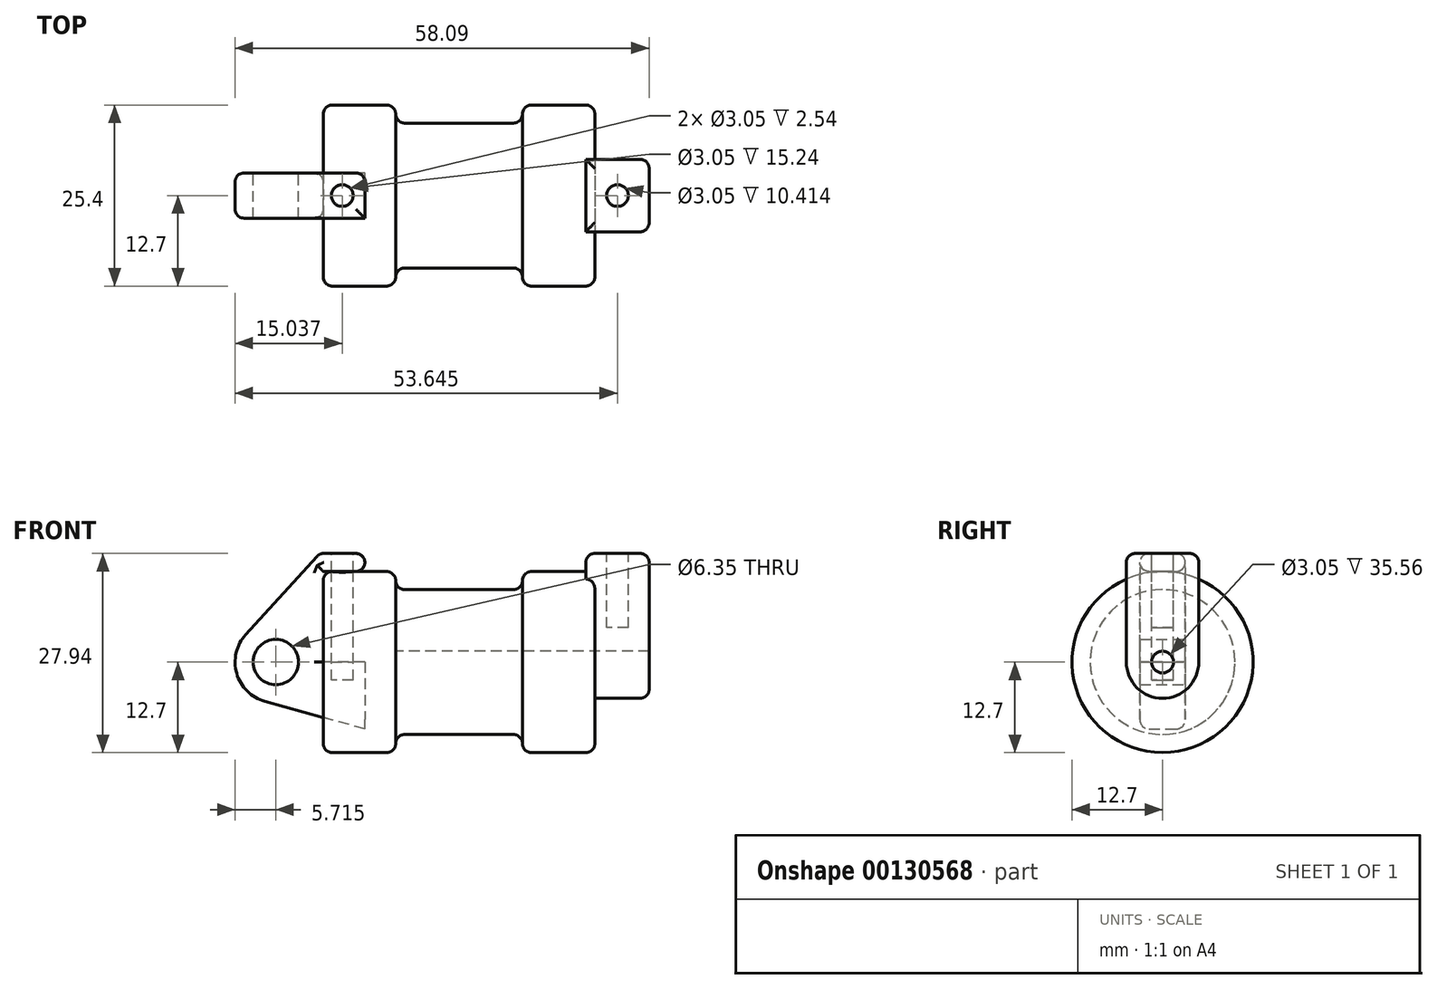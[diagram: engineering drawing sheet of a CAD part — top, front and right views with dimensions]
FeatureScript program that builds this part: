
annotation { "Feature Type Name" : "Feature", "Feature Type Description" : "" }
export const myFeature = defineFeature(function(context is Context, id is Id, definition is map)
    precondition{}
    {
        {
            var Q0;
            Q0=qCreatedBy(makeId("Front.planeOp"),FACE);
            var sketch = newSketch(context, id + "F0", { "sketchPlane" : qUnion([Q0])});
            skLineSegment(sketch, "E0", {"start": v(0, 0) * mm, "end": v(0, 12.7) * mm});
            skLineSegment(sketch, "E1", {"start": v(0, 12.7) * mm, "end": v(10.16, 12.7) * mm});
            skLineSegment(sketch, "E2", {"start": v(10.16, 12.7) * mm, "end": v(10.16, 10.16) * mm});
            skLineSegment(sketch, "E3", {"start": v(10.16, 10.16) * mm, "end": v(27.94, 10.16) * mm});
            skLineSegment(sketch, "E4", {"start": v(27.94, 10.16) * mm, "end": v(27.94, 12.7) * mm});
            skLineSegment(sketch, "E5", {"start": v(27.94, 12.7) * mm, "end": v(38.1, 12.7) * mm});
            skLineSegment(sketch, "E6", {"start": v(38.1, 12.7) * mm, "end": v(38.1, 0) * mm});
            skLineSegment(sketch, "E7", {"start": v(38.1, 0) * mm, "end": v(0, 0) * mm});
            skLineSegment(sketch, "E8", {"start": v(5.84, 15.24) * mm, "end": v(-0.5, 15.24) * mm});
            skLineSegment(sketch, "E9", {"start": v(-0.5, 15.24) * mm, "end": v(-10.88, 3.85) * mm});
            skLineSegment(sketch, "E10", {"start": v(0, 0) * mm, "end": v(-6.65, 0) * mm});
            skCircle(sketch, "E11", {"center": v(-6.65, 0) * mm, "radius": 5.72 * mm});
            skCircle(sketch, "E12", {"center": v(-6.65, 0) * mm, "radius": 3.18 * mm});
            skLineSegment(sketch, "E13", {"start": v(5.84, 15.24) * mm, "end": v(5.84, -9.4) * mm});
            skLineSegment(sketch, "E14", {"start": v(5.84, -9.4) * mm, "end": v(-8.18, -5.5) * mm});
            skSolve(sketch);
        }
        {
            var Q0;
            {var subQ0=sQuery(id+"F0.wireOp",EDGE,"E0");Q0=makeQuery(id+"F0.imprint","IMPRINT",FACE,{"disambiguationData":[TD([[makeQuery(id+"F0.imprint","IMPRINT",EDGE,{"derivedFrom":subQ0}),-1.0]])]});}
            var Q1;
            {var subQ0=sQuery(id+"F0.wireOp",EDGE,"E2");Q1=makeQuery(id+"F0.imprint","IMPRINT",FACE,{"disambiguationData":[TD([[makeQuery(id+"F0.imprint","IMPRINT",EDGE,{"derivedFrom":subQ0}),-1.0]])]});}
            var Q2;
            Q2=sQuery(id+"F0.wireOp",EDGE,"E7");
            revolve(context, id + "F1", {"entities" : qUnion([Q0, Q1]), "axis" : qUnion([Q2]), "revolveType" : RevolveType.FULL});
        }
        {
            var Q0;
            {var subQ3=sQuery(id+"F0.wireOp",EDGE,"E0");Q0=makeQuery(id+"F0.imprint","IMPRINT",FACE,{"disambiguationData":[TD([[makeQuery(id+"F0.imprint","IMPRINT",EDGE,{"derivedFrom":subQ3}),1.0]])]});}
            var Q1;
            {var subQ0=sQuery(id+"F0.wireOp",EDGE,"E14");Q1=makeQuery(id+"F0.imprint","IMPRINT",FACE,{"disambiguationData":[TD([[makeQuery(id+"F0.imprint","IMPRINT",EDGE,{"derivedFrom":subQ0}),-1.0]])]});}
            var Q2;
            {var subQ4=sQuery(id+"F0.wireOp",EDGE,"E12");Q2=makeQuery(id+"F0.imprint","IMPRINT",FACE,{"disambiguationData":[TD([[makeQuery(id+"F0.imprint","IMPRINT",EDGE,{"derivedFrom":subQ4}),-1.0]])]});}
            extrude(context, id + "F2", {"entities" : qUnion([Q0, Q1, Q2]), "endBound" : BoundingType.SYMMETRIC, "depth" : 6.35 * mm});
        }
        {
            var Q0;
            Q0=makeQuery(id+"F1.opRevolve","SWEPT_FACE",FACE,{"disambiguationData":[OSD([sQuery(id+"F0.wireOp",EDGE,"E6")])]});
            var sketch = newSketch(context, id + "F3", { "sketchPlane" : qUnion([Q0])});
            skCircle(sketch, "E15", {"center": v(0, 0) * mm, "radius": 1.52 * mm});
            skCircle(sketch, "E16", {"center": v(0, 0) * mm, "radius": 5.08 * mm});
            skLineSegment(sketch, "E17", {"start": v(-5.08, 0) * mm, "end": v(-5.08, 15.24) * mm});
            skLineSegment(sketch, "E18", {"start": v(5.08, 0) * mm, "end": v(5.08, 15.24) * mm});
            skLineSegment(sketch, "E19", {"start": v(-5.08, 15.24) * mm, "end": v(5.08, 15.24) * mm});
            skSolve(sketch);
        }
        {
            var Q0;
            {var subQ0=sQuery(id+"F3.wireOp",EDGE,"E19");Q0=makeQuery(id+"F3.imprint","IMPRINT",FACE,{"disambiguationData":[TD([[makeQuery(id+"F3.imprint","IMPRINT",EDGE,{"derivedFrom":subQ0}),-1.0]])]});}
            var Q1;
            {var subQ0=sQuery(id+"F3.wireOp",EDGE,"E17");var subQ1=sQuery(id+"F3.wireOp",EDGE,"E16");var subQ2=makeQuery(id+"F3.imprint","INTERSECT",VERTEX,{"derivedFrom":[subQ1,subQ0]});Q1=makeQuery(id+"F3.imprint","IMPRINT",FACE,{"disambiguationData":[TD([[makeQuery(id+"F3.imprint","IMPRINT",EDGE,{"disambiguationData":[TD([[subQ2,1.0]])],"derivedFrom":subQ1}),-1.0]])]});}
            var Q2;
            Q2=makeQuery(id+"F3.imprint","IMPRINT",FACE,{"disambiguationData":[TD([[makeQuery(id+"F3.imprint","IMPRINT",EDGE,{"derivedFrom":sQuery(id+"F3.wireOp",EDGE,"E15")}),-1.0]])]});
            extrude(context, id + "F4", {"entities" : qUnion([Q0, Q1, Q2]), "operationType" : NewBodyOperationType.ADD, "depth" : 7.62 * mm, "hasSecondDirection" : true, "secondDirectionOppositeDirection" : true, "secondDirectionDepth" : 1.27 * mm});
        }
        {
            var Q0;
            Q0=makeQuery(id+"F4.boolean.opBoolean","SPLIT",FACE,{"disambiguationData":[TD([makeQuery(id+"F4.opExtrude","SWEPT_FACE",FACE,{"disambiguationData":[OSD([sQuery(id+"F3.wireOp",EDGE,"E15")])]})])],"derivedFrom":makeQuery(id+"F1.opRevolve","SWEPT_FACE",FACE,{"disambiguationData":[OSD([sQuery(id+"F0.wireOp",EDGE,"E6")])]})});
            var Q1;
            Q1=makeQuery(id+"F1.opRevolve","SWEPT_FACE",FACE,{"disambiguationData":[OSD([sQuery(id+"F0.wireOp",EDGE,"E2")])]});
            extrude(context, id + "F5", {"entities" : qUnion([Q0]), "operationType" : NewBodyOperationType.REMOVE, "endBound" : BoundingType.UP_TO_SURFACE, "oppositeDirection" : true, "endBoundEntityFace" : qUnion([Q1]), "depth" : 25.4 * mm});
        }
        {
            var Q0;
            Q0=makeQuery(id+"F2.opExtrude","SWEPT_FACE",FACE,{"disambiguationData":[OSD([sQuery(id+"F0.wireOp",EDGE,"E8")])]});
            var sketch = newSketch(context, id + "F6", { "sketchPlane" : qUnion([Q0])});
            skCircle(sketch, "E20", {"center": v(2.67, 0) * mm, "radius": 1.52 * mm});
            skPoint(sketch, "E20.centerSnap0", {"position": v(2.67, -3.18) * mm});
            skPoint(sketch, "E20.centerSnap1", {"position": v(-0.5, 0) * mm});
            skSolve(sketch);
        }
        {
            var Q0;
            Q0=makeQuery(id+"F4.opExtrude","SWEPT_FACE",FACE,{"disambiguationData":[OSD([sQuery(id+"F3.wireOp",EDGE,"E19")])]});
            var sketch = newSketch(context, id + "F7", { "sketchPlane" : qUnion([Q0])});
            skCircle(sketch, "E21", {"center": v(41.28, 0) * mm, "radius": 1.52 * mm});
            skPoint(sketch, "E21.centerSnap0", {"position": v(41.28, -5.08) * mm});
            skPoint(sketch, "E21.centerSnap1", {"position": v(45.72, 0) * mm});
            skSolve(sketch);
        }
        {
            var Q0;
            Q0=makeQuery(id+"F6.imprint","IMPRINT",FACE,{"disambiguationData":[TD([[makeQuery(id+"F6.imprint","IMPRINT",EDGE,{"derivedFrom":sQuery(id+"F6.wireOp",EDGE,"E20")}),1.0]])]});
            extrude(context, id + "F8", {"entities" : qUnion([Q0]), "operationType" : NewBodyOperationType.REMOVE, "oppositeDirection" : true, "depth" : 17.78 * mm});
        }
        {
            var Q0;
            Q0=makeQuery(id+"F7.imprint","IMPRINT",FACE,{"disambiguationData":[TD([[makeQuery(id+"F7.imprint","IMPRINT",EDGE,{"derivedFrom":sQuery(id+"F7.wireOp",EDGE,"E21")}),1.0]])]});
            var Q1;
            Q1=sQuery(id+"F7.wireOp",EDGE,"E21");
            extrude(context, id + "F9", {"entities" : qUnion([Q0]), "operationType" : NewBodyOperationType.REMOVE, "surfaceEntities" : qUnion([Q1]), "oppositeDirection" : true, "depth" : 10.4 * mm});
        }
        {
            var Q0;
            Q0=makeQuery(id+"F1.opRevolve","SWEPT_EDGE",EDGE,{"disambiguationData":[OSD([sQuery(id+"F0.wireOp",EDGE,"E4"),sQuery(id+"F0.wireOp",EDGE,"E5")])]});
            var Q1;
            Q1=makeQuery(id+"F1.opRevolve","SWEPT_EDGE",EDGE,{"disambiguationData":[OSD([sQuery(id+"F0.wireOp",EDGE,"E5"),sQuery(id+"F0.wireOp",EDGE,"E6")])]});
            var Q2;
            Q2=makeQuery(id+"F1.opRevolve","SWEPT_EDGE",EDGE,{"disambiguationData":[OSD([sQuery(id+"F0.wireOp",EDGE,"E0"),sQuery(id+"F0.wireOp",EDGE,"E1")])]});
            var Q3;
            Q3=makeQuery(id+"F1.opRevolve","SWEPT_EDGE",EDGE,{"disambiguationData":[OSD([sQuery(id+"F0.wireOp",EDGE,"E1"),sQuery(id+"F0.wireOp",EDGE,"E2")])]});
            fillet(context, id + "F10", {"entities" : qUnion([Q0, Q1, Q2, Q3]), "radius" : 1.27 * mm, "tangentPropagation" : true, "allowEdgeOverflow" : false});
        }
        {
            var Q0;
            Q0=makeQuery(id+"F4.opExtrude","CAP_EDGE",EDGE,{"disambiguationData":[OSD([sQuery(id+"F3.wireOp",EDGE,"E18")])],"isStart":false});
            var Q1;
            Q1=makeQuery(id+"F4.opExtrude","CAP_EDGE",EDGE,{"disambiguationData":[OSD([sQuery(id+"F3.wireOp",EDGE,"E17")])],"isStart":false});
            var Q2;
            Q2=makeQuery(id+"F4.opExtrude","SWEPT_EDGE",EDGE,{"disambiguationData":[OSD([sQuery(id+"F3.wireOp",EDGE,"E18"),sQuery(id+"F3.wireOp",EDGE,"E19")])]});
            var Q3;
            Q3=makeQuery(id+"F4.opExtrude","SWEPT_EDGE",EDGE,{"disambiguationData":[OSD([sQuery(id+"F3.wireOp",EDGE,"E17"),sQuery(id+"F3.wireOp",EDGE,"E19")])]});
            var Q4;
            Q4=makeQuery(id+"F4.opExtrude","CAP_EDGE",EDGE,{"disambiguationData":[OSD([sQuery(id+"F3.wireOp",EDGE,"E19")])],"isStart":true});
            var Q5;
            Q5=makeQuery(id+"F4.opExtrude","CAP_EDGE",EDGE,{"disambiguationData":[OSD([sQuery(id+"F3.wireOp",EDGE,"E19")])],"isStart":false});
            var Q6;
            {var subQ0=sQuery(id+"F0.wireOp",EDGE,"E2");Q6=makeQuery(id+"F10.opFillet","BLEND_EDGE",EDGE,{"blendedFrom":[makeQuery(id+"F1.opRevolve","SWEPT_EDGE",EDGE,{"disambiguationData":[OSD([sQuery(id+"F0.wireOp",EDGE,"E1"),subQ0])]}),makeQuery(id+"F1.opRevolve","SWEPT_FACE",FACE,{"disambiguationData":[OSD([subQ0])]})],"blendedInto":[makeQuery(id+"F1.opRevolve","SWEPT_FACE",FACE,{"disambiguationData":[OSD([subQ0])]})]});}
            var Q7;
            Q7=makeQuery(id+"F1.opRevolve","SWEPT_EDGE",EDGE,{"disambiguationData":[OSD([sQuery(id+"F0.wireOp",EDGE,"E3"),sQuery(id+"F0.wireOp",EDGE,"E4")])]});
            var Q8;
            Q8=makeQuery(id+"F2.opExtrude","CAP_EDGE",EDGE,{"disambiguationData":[OSD([sQuery(id+"F0.wireOp",EDGE,"E9")])],"isStart":false});
            var Q9;
            Q9=makeQuery(id+"F2.opExtrude","CAP_EDGE",EDGE,{"disambiguationData":[OSD([sQuery(id+"F0.wireOp",EDGE,"E8")])],"isStart":false});
            var Q10;
            Q10=makeQuery(id+"F2.opExtrude","CAP_EDGE",EDGE,{"disambiguationData":[OSD([sQuery(id+"F0.wireOp",EDGE,"E1")])],"isStart":false});
            var Q11;
            Q11=makeQuery(id+"F2.opExtrude","SWEPT_EDGE",EDGE,{"disambiguationData":[OSD([sQuery(id+"F0.wireOp",EDGE,"E8"),sQuery(id+"F0.wireOp",EDGE,"E9")])]});
            var Q12;
            Q12=makeQuery(id+"F2.opExtrude","CAP_EDGE",EDGE,{"disambiguationData":[OSD([sQuery(id+"F0.wireOp",EDGE,"E8")])],"isStart":true});
            var Q13;
            Q13=makeQuery(id+"F2.opExtrude","CAP_EDGE",EDGE,{"disambiguationData":[OSD([sQuery(id+"F0.wireOp",EDGE,"E1")])],"isStart":true});
            var Q14;
            Q14=makeQuery(id+"F2.opExtrude","CAP_EDGE",EDGE,{"disambiguationData":[OSD([sQuery(id+"F0.wireOp",EDGE,"E11")])],"isStart":false});
            var Q15;
            Q15=makeQuery(id+"F2.opExtrude","CAP_EDGE",EDGE,{"disambiguationData":[OSD([sQuery(id+"F0.wireOp",EDGE,"E14")])],"isStart":false});
            var Q16;
            Q16=makeQuery(id+"F2.opExtrude","CAP_EDGE",EDGE,{"disambiguationData":[OSD([sQuery(id+"F0.wireOp",EDGE,"E0")])],"isStart":false});
            var Q17;
            Q17=makeQuery(id+"F2.opExtrude","CAP_EDGE",EDGE,{"disambiguationData":[OSD([sQuery(id+"F0.wireOp",EDGE,"E0")])],"isStart":true});
            var Q18;
            Q18=makeQuery(id+"F2.opExtrude","CAP_EDGE",EDGE,{"disambiguationData":[OSD([sQuery(id+"F0.wireOp",EDGE,"E11")])],"isStart":true});
            var Q19;
            Q19=makeQuery(id+"F2.opExtrude","CAP_EDGE",EDGE,{"disambiguationData":[OSD([sQuery(id+"F0.wireOp",EDGE,"E14")])],"isStart":true});
            var Q20;
            {var subQ0=sQuery(id+"F0.wireOp",EDGE,"E13");Q20=makeQuery(id+"F2.opExtrude","CAP_EDGE",EDGE,{"disambiguationData":[OSD([subQ0]),TDD([makeQuery(id+"F0.imprint","IMPRINT",EDGE,{"disambiguationData":[TD([[makeQuery(id+"F0.imprint","INTERSECT",VERTEX,{"derivedFrom":[sQuery(id+"F0.wireOp",EDGE,"E8"),subQ0]}),-1.0]])],"derivedFrom":subQ0})])],"isStart":true});}
            var Q21;
            Q21=makeQuery(id+"F2.opExtrude","SWEPT_EDGE",EDGE,{"disambiguationData":[OSD([sQuery(id+"F0.wireOp",EDGE,"E8"),sQuery(id+"F0.wireOp",EDGE,"E13")])]});
            var Q22;
            Q22=makeQuery(id+"F2.opExtrude","SWEPT_EDGE",EDGE,{"disambiguationData":[OSD([sQuery(id+"F0.wireOp",EDGE,"E1"),sQuery(id+"F0.wireOp",EDGE,"E13")])]});
            var Q23;
            Q23=makeQuery(id+"F1.opRevolve","SWEPT_EDGE",EDGE,{"disambiguationData":[OSD([sQuery(id+"F0.wireOp",EDGE,"E2"),sQuery(id+"F0.wireOp",EDGE,"E3")])]});
            fillet(context, id + "F11", {"entities" : qUnion([Q0, Q1, Q2, Q3, Q4, Q5, Q6, Q7, Q8, Q9, Q10, Q11, Q12, Q13, Q14, Q15, Q16, Q17, Q18, Q19, Q20, Q21, Q22, Q23]), "radius" : 1.27 * mm, "tangentPropagation" : true, "allowEdgeOverflow" : false});
        }
    });
